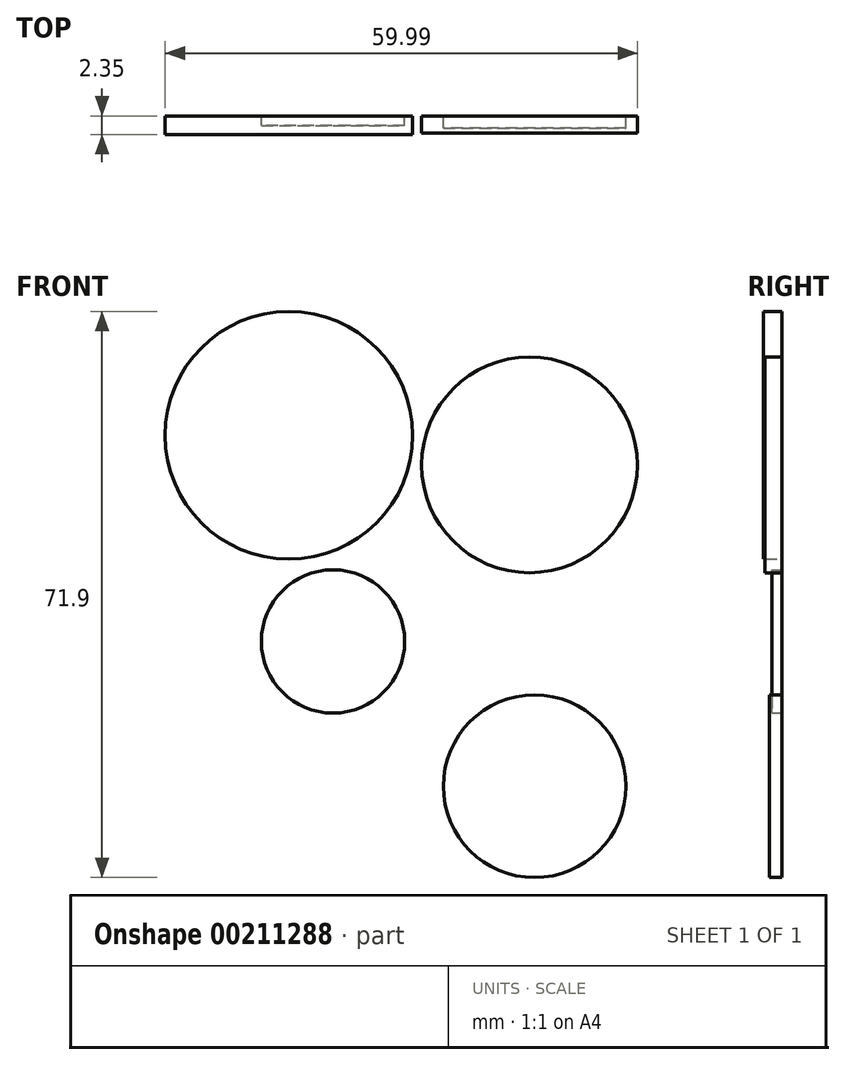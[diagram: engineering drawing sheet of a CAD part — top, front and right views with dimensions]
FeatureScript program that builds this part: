
annotation { "Feature Type Name" : "Feature", "Feature Type Description" : "" }
export const myFeature = defineFeature(function(context is Context, id is Id, definition is map)
    precondition{}
    {
        {
            var Q0;
            Q0=qCreatedBy(makeId("Front.planeOp"),FACE);
            var sketch = newSketch(context, id + "F0", { "sketchPlane" : qUnion([Q0])});
            skCircle(sketch, "E0", {"center": v(23.96, 9.3) * mm, "radius": 15.72 * mm});
            skSolve(sketch);
        }
        {
            var Q0;
            Q0 = qSketchRegion(id + "F0", true);
            extrude(context, id + "F1", {"entities" : qUnion([Q0]), "depth" : 2.35 * mm});
        }
        {
            var Q0;
            Q0=qCreatedBy(makeId("Front.planeOp"),FACE);
            var sketch = newSketch(context, id + "F2", { "sketchPlane" : qUnion([Q0])});
            skCircle(sketch, "E1", {"center": v(54.52, 5.55) * mm, "radius": 13.7 * mm});
            skSolve(sketch);
        }
        {
            var Q0;
            Q0 = qSketchRegion(id + "F2", true);
            extrude(context, id + "F3", {"entities" : qUnion([Q0]), "depth" : 2.15 * mm});
        }
        {
            var Q0;
            Q0=qCreatedBy(makeId("Front.planeOp"),FACE);
            var sketch = newSketch(context, id + "F4", { "sketchPlane" : qUnion([Q0])});
            skCircle(sketch, "E2", {"center": v(55.16, -35.27) * mm, "radius": 11.6 * mm});
            skSolve(sketch);
        }
        {
            var Q0;
            Q0 = qSketchRegion(id + "F4", true);
            extrude(context, id + "F5", {"entities" : qUnion([Q0]), "depth" : 1.55 * mm});
        }
        {
            var Q0;
            Q0=qCreatedBy(makeId("Front.planeOp"),FACE);
            var sketch = newSketch(context, id + "F6", { "sketchPlane" : qUnion([Q0])});
            skCircle(sketch, "E3", {"center": v(29.55, -16.88) * mm, "radius": 9.1 * mm});
            skSolve(sketch);
        }
        {
            var Q0;
            Q0 = qSketchRegion(id + "F6", true);
            extrude(context, id + "F7", {"entities" : qUnion([Q0]), "depth" : 1.25 * mm});
        }
    });
